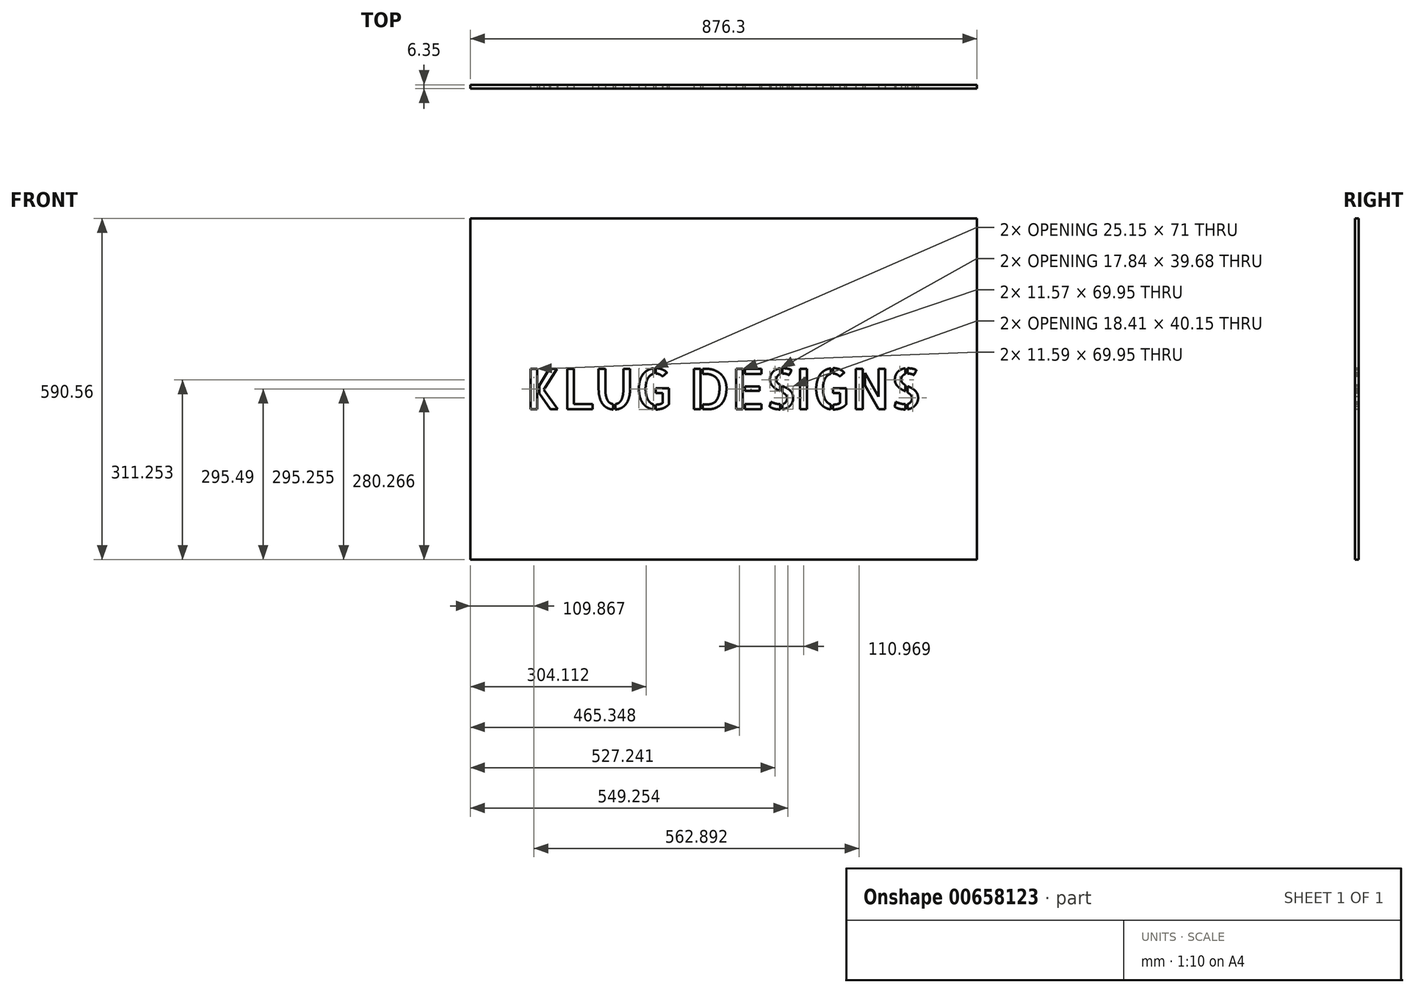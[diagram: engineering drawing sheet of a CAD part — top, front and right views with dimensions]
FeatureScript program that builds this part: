
annotation { "Feature Type Name" : "Feature", "Feature Type Description" : "" }
export const myFeature = defineFeature(function(context is Context, id is Id, definition is map)
    precondition{}
    {
        {
            var Q0;
            Q0=qCreatedBy(makeId("Front.planeOp"),FACE);
            var sketch = newSketch(context, id + "F0", { "sketchPlane" : qUnion([Q0])});
            skLineSegment(sketch, "E0.bottom", {"start": v(438.15, 295.28) * mm, "end": v(-438.15, 295.28) * mm});
            skLineSegment(sketch, "E0.top", {"start": v(438.15, -295.28) * mm, "end": v(-438.15, -295.28) * mm});
            skLineSegment(sketch, "E0.left", {"start": v(438.15, 295.28) * mm, "end": v(438.15, -295.28) * mm});
            skLineSegment(sketch, "E0.right", {"start": v(-438.15, 295.28) * mm, "end": v(-438.15, -295.28) * mm});
            skPoint(sketch, "E0.middle", {"position": v(0, 0) * mm});
            skSolve(sketch);
        }
        {
            var Q0;
            Q0=qSketchRegion(id+"F0",true);
            extrude(context, id + "F1", {"entities" : qUnion([Q0]), "depth" : 6.35 * mm, "offsetDistance" : 25.4 * mm});
        }
        {
            var Q0;
            Q0=makeQuery(id+"F1.opExtrude","CAP_FACE",FACE,{"disambiguationData":[OSD([sQuery(id+"F0.wireOp",EDGE,"E0.bottom"),sQuery(id+"F0.wireOp",EDGE,"E0.top"),sQuery(id+"F0.wireOp",EDGE,"E0.left"),sQuery(id+"F0.wireOp",EDGE,"E0.right")])],"isStart":false});
            var sketch = newSketch(context, id + "F2", { "sketchPlane" : qUnion([Q0])});
            skText(sketch, "E1", { "text": "KLUG DESIGNS", "fontName": "AllertaStencil-Regular.ttf"});
            skLineSegment(sketch, "E2", {"start": v(-342.9, 0) * mm, "end": v(342.9, 0) * mm, "construction": true});
            const initialGuessF2  = {"E1": [-0.3429, -0.035, 1, 0, 0.06998]};
            skSetInitialGuess(sketch, initialGuessF2);
            skSolve(sketch);
        }
        {
            var Q0;
            Q0 = qSketchRegion(id + "F2", true);
            extrude(context, id + "F3", {"entities" : qUnion([Q0]), "operationType" : NewBodyOperationType.REMOVE, "endBound" : BoundingType.THROUGH_ALL, "oppositeDirection" : true, "depth" : 25.4 * mm, "offsetDistance" : 25.4 * mm});
        }
        {
            var Q0;
            Q0 = qSketchRegion(id + "F2", true);
            extrude(context, id + "F4", {"entities" : qUnion([Q0]), "operationType" : NewBodyOperationType.REMOVE, "oppositeDirection" : true, "depth" : 25.4 * mm, "offsetDistance" : 25.4 * mm});
        }
    });
